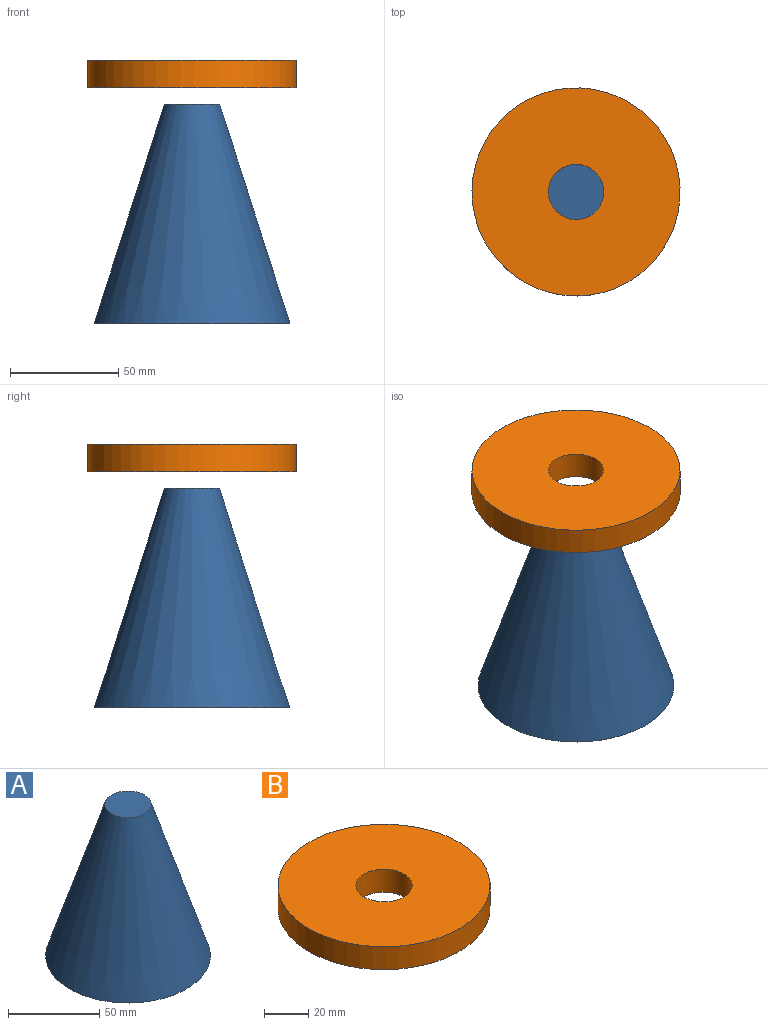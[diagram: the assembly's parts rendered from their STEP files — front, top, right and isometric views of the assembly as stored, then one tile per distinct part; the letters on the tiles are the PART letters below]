
ASSEMBLY  parts=2 mates=2
PART A: 5 faces, bbox 90.5x90.5x101.6 mm
  f0: plane 90.53x90.53mm, normal (0,0,-1), area 1427.6mm2, adj f2,f4
  f1: plane 25.53x25.53mm, normal (0,0,1), area 511.9mm2, adj f2
  f2: cone r=45.27mm half-angle=17.7deg, axis (0,0,-1), area 19447.1mm2, adj f0,f1
  f3: plane 18.11x18.11mm, normal (0,0,-1), area 257.6mm2, adj f4
  f4: cone r=40.43mm half-angle=17.7deg, axis (0,0,-1), area 15596mm2, adj f0,f3
PART B: 4 faces, bbox 96.2x96.2x12.7 mm
  f0: cylinder r=12.76mm len=25.53mm, axis (0,0,-1), area 1018.6mm2, adj f2,f3
  f1: cylinder r=48.1mm len=96.19mm, axis (0,0,-1), area 3838mm2, adj f2,f3
  f2: plane 96.19x96.19mm, normal (0,0,1), area 6755.8mm2, adj f0,f1
  f3: plane 96.19x96.19mm, normal (0,0,-1), area 6755.8mm2, adj f0,f1
PLACE A t=(28.64,17.04,0)mm fixed
PLACE B rot(axis=(0,0,-1),145.5deg) t=(28.64,17.04,7.62)mm
MATE cylindrical B.f1 <-> A.f2  axis (0,0,-1) through (28.64,17.04,115.57)mm
MATE planar B.f1 <-> A.f2  axis (0,0,-1) through (28.64,17.04,109.22)mm
